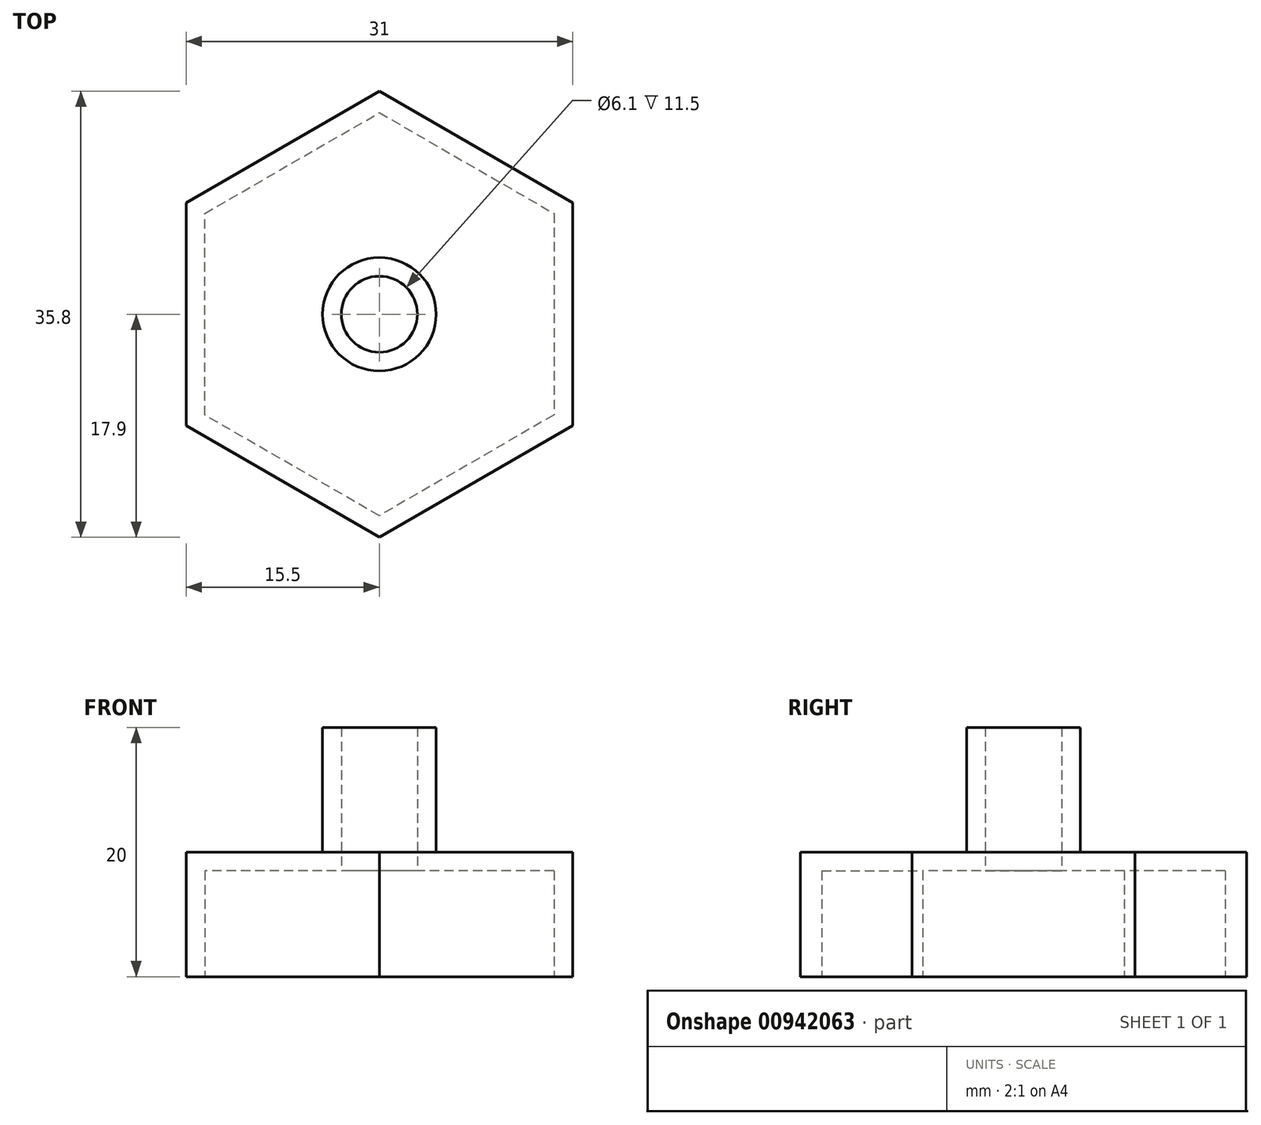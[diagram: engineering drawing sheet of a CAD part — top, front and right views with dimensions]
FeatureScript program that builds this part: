
annotation { "Feature Type Name" : "Feature", "Feature Type Description" : "" }
export const myFeature = defineFeature(function(context is Context, id is Id, definition is map)
    precondition{}
    {
        {
            var Q0;
            Q0=qCreatedBy(makeId("Top.planeOp"),FACE);
            var sketch = newSketch(context, id + "F0", { "sketchPlane" : qUnion([Q0])});
            skCircle(sketch, "E0.cCircle", {"center": v(0, 0) * mm, "radius": 17.9 * mm, "construction": true});
            skLineSegment(sketch, "E0.0", {"start": v(0, -17.9) * mm, "end": v(-15.5, -8.95) * mm});
            skLineSegment(sketch, "E0.1", {"start": v(-15.5, -8.95) * mm, "end": v(-15.5, 8.95) * mm});
            skLineSegment(sketch, "E0.2", {"start": v(-15.5, 8.95) * mm, "end": v(0, 17.9) * mm});
            skLineSegment(sketch, "E0.3", {"start": v(0, 17.9) * mm, "end": v(15.5, 8.95) * mm});
            skLineSegment(sketch, "E0.4", {"start": v(15.5, 8.95) * mm, "end": v(15.5, -8.95) * mm});
            skLineSegment(sketch, "E0.5", {"start": v(15.5, -8.95) * mm, "end": v(0, -17.9) * mm});
            skSolve(sketch);
        }
        {
            var Q0;
            Q0=qSketchRegion(id+"F0",true);
            extrude(context, id + "F1", {"entities" : qUnion([Q0]), "depth" : 10 * mm});
        }
        {
            var Q0;
            Q0=makeQuery(id+"F1.opExtrude","CAP_FACE",FACE,{"disambiguationData":[OSD([sQuery(id+"F0.wireOp",EDGE,"E0.0"),sQuery(id+"F0.wireOp",EDGE,"E0.1"),sQuery(id+"F0.wireOp",EDGE,"E0.2"),sQuery(id+"F0.wireOp",EDGE,"E0.3"),sQuery(id+"F0.wireOp",EDGE,"E0.4"),sQuery(id+"F0.wireOp",EDGE,"E0.5")])],"isStart":false});
            var sketch = newSketch(context, id + "F2", { "sketchPlane" : qUnion([Q0])});
            skCircle(sketch, "E1", {"center": v(0, 0) * mm, "radius": 4.55 * mm});
            skSolve(sketch);
        }
        {
            var Q0;
            Q0=makeQuery(id+"F2.imprint","IMPRINT",FACE,{"disambiguationData":[TD([[makeQuery(id+"F2.imprint","IMPRINT",EDGE,{"derivedFrom":sQuery(id+"F2.wireOp",EDGE,"E1")}),1.0]])]});
            extrude(context, id + "F3", {"entities" : qUnion([Q0]), "operationType" : NewBodyOperationType.ADD, "endBound" : BoundingType.SYMMETRIC, "depth" : 20 * mm});
        }
        {
            var Q0;
            Q0=makeQuery(id+"F1.opExtrude","CAP_FACE",FACE,{"disambiguationData":[OSD([sQuery(id+"F0.wireOp",EDGE,"E0.0"),sQuery(id+"F0.wireOp",EDGE,"E0.1"),sQuery(id+"F0.wireOp",EDGE,"E0.2"),sQuery(id+"F0.wireOp",EDGE,"E0.3"),sQuery(id+"F0.wireOp",EDGE,"E0.4"),sQuery(id+"F0.wireOp",EDGE,"E0.5")])],"isStart":true});
            var Q1;
            Q1=makeQuery(id+"F3.opExtrude","CAP_FACE",FACE,{"disambiguationData":[OSD([sQuery(id+"F2.wireOp",EDGE,"E1")])],"isStart":false});
            shell(context, id + "F4", {"entities" : qUnion([Q0, Q1]), "thickness" : 1.5 * mm});
        }
    });
